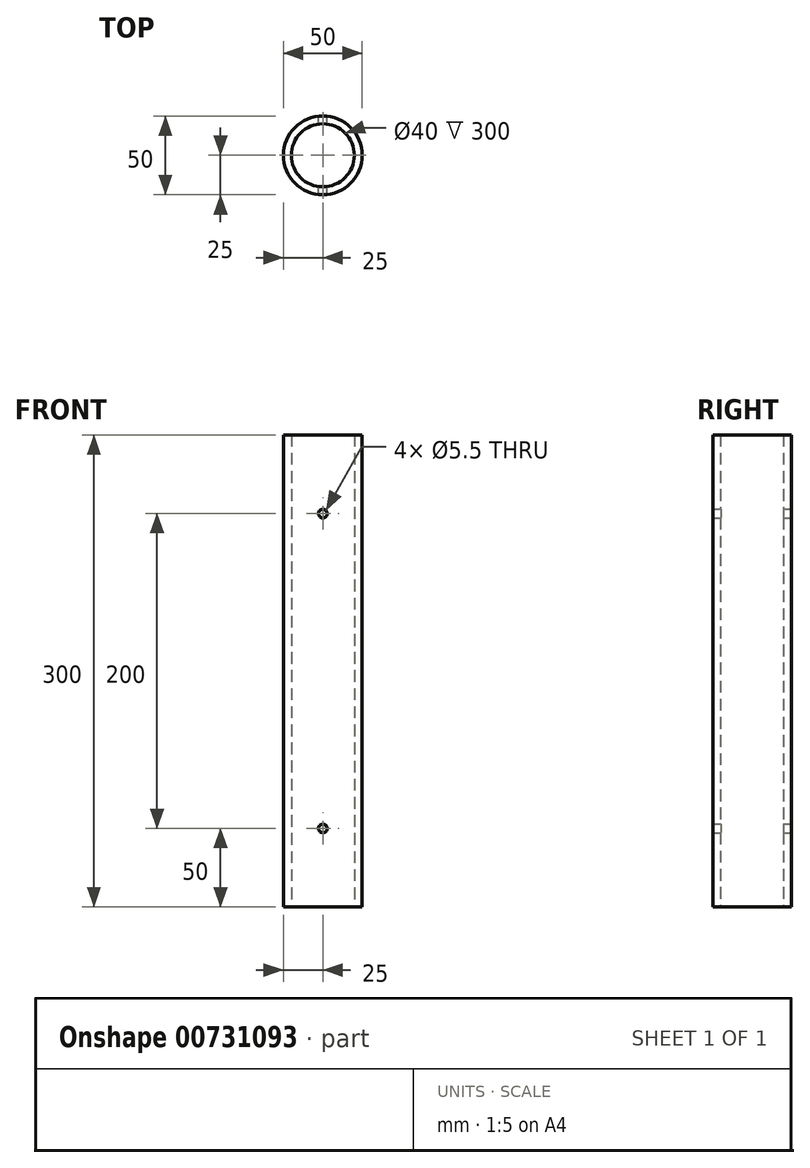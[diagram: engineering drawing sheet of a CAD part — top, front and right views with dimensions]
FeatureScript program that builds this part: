
annotation { "Feature Type Name" : "Feature", "Feature Type Description" : "" }
export const myFeature = defineFeature(function(context is Context, id is Id, definition is map)
    precondition{}
    {
        {
            var Q0;
            Q0=qCreatedBy(makeId("Top.planeOp"),FACE);
            var sketch = newSketch(context, id + "F0", { "sketchPlane" : qUnion([Q0])});
            skCircle(sketch, "E0", {"center": v(0, 0) * mm, "radius": 25 * mm});
            skPoint(sketch, "E1", {"position": v(0, 25) * mm});
            skSolve(sketch);
        }
        {
            var Q0;
            Q0=makeQuery(id+"F0.imprint","IMPRINT",FACE,{"disambiguationData":[TD([[makeQuery(id+"F0.imprint","IMPRINT",EDGE,{"derivedFrom":sQuery(id+"F0.wireOp",EDGE,"E0")}),1.0]])]});
            extrude(context, id + "F1", {"entities" : qUnion([Q0]), "endBound" : BoundingType.SYMMETRIC, "depth" : 300 * mm, "offsetDistance" : 25 * mm});
        }
        {
            var Q0;
            Q0=makeQuery(id+"F1.opExtrude","CAP_FACE",FACE,{"disambiguationData":[OSD([sQuery(id+"F0.wireOp",EDGE,"E0")])],"isStart":false});
            var Q1;
            Q1=makeQuery(id+"F1.opExtrude","CAP_FACE",FACE,{"disambiguationData":[OSD([sQuery(id+"F0.wireOp",EDGE,"E0")])],"isStart":true});
            shell(context, id + "F2", {"entities" : qUnion([Q0, Q1]), "thickness" : 5 * mm});
        }
        {
            var Q0;
            Q0=qCreatedBy(makeId("Front.planeOp"),FACE);
            cPlane(context, id + "F3", {"entities" : qUnion([Q0]), "cplaneType" : CPlaneType.OFFSET, "offset" : 50 * mm, "oppositeDirection" : true, "width" : 150 * mm, "height" : 150 * mm});
        }
        {
            var Q0;
            Q0=qCreatedBy(id+"F3.planeOp",FACE);
            var sketch = newSketch(context, id + "F4", { "sketchPlane" : qUnion([Q0])});
            skPoint(sketch, "E2", {"position": v(0, 100) * mm});
            skPoint(sketch, "E3", {"position": v(0, -100) * mm});
            skSolve(sketch);
        }
        {
            var Q0;
            Q0=sQuery(id+"F4.wireOp",VERTEX,"E2");
            var Q1;
            Q1=sQuery(id+"F4.wireOp",VERTEX,"E3");
            var Q2;
            Q2=makeQuery(id+"F1.opExtrude","SWEPT_BODY",BODY,{"disambiguationData":[OSD([sQuery(id+"F0.wireOp",EDGE,"E0")])]});
            hole(context, id + "F5", {"style" : HoleStyle.SIMPLE, "endStyle" : HoleEndStyle.THROUGH, "oppositeDirection" : true, "holeDiameter" : 5.5 * mm, "majorDiameter" : 5 * mm, "isTappedThrough" : true, "tappedDepth" : 12 * mm, "tapClearance" : 3, "locations" : qUnion([Q0, Q1]), "scope" : qUnion([Q2])});
        }
    });
